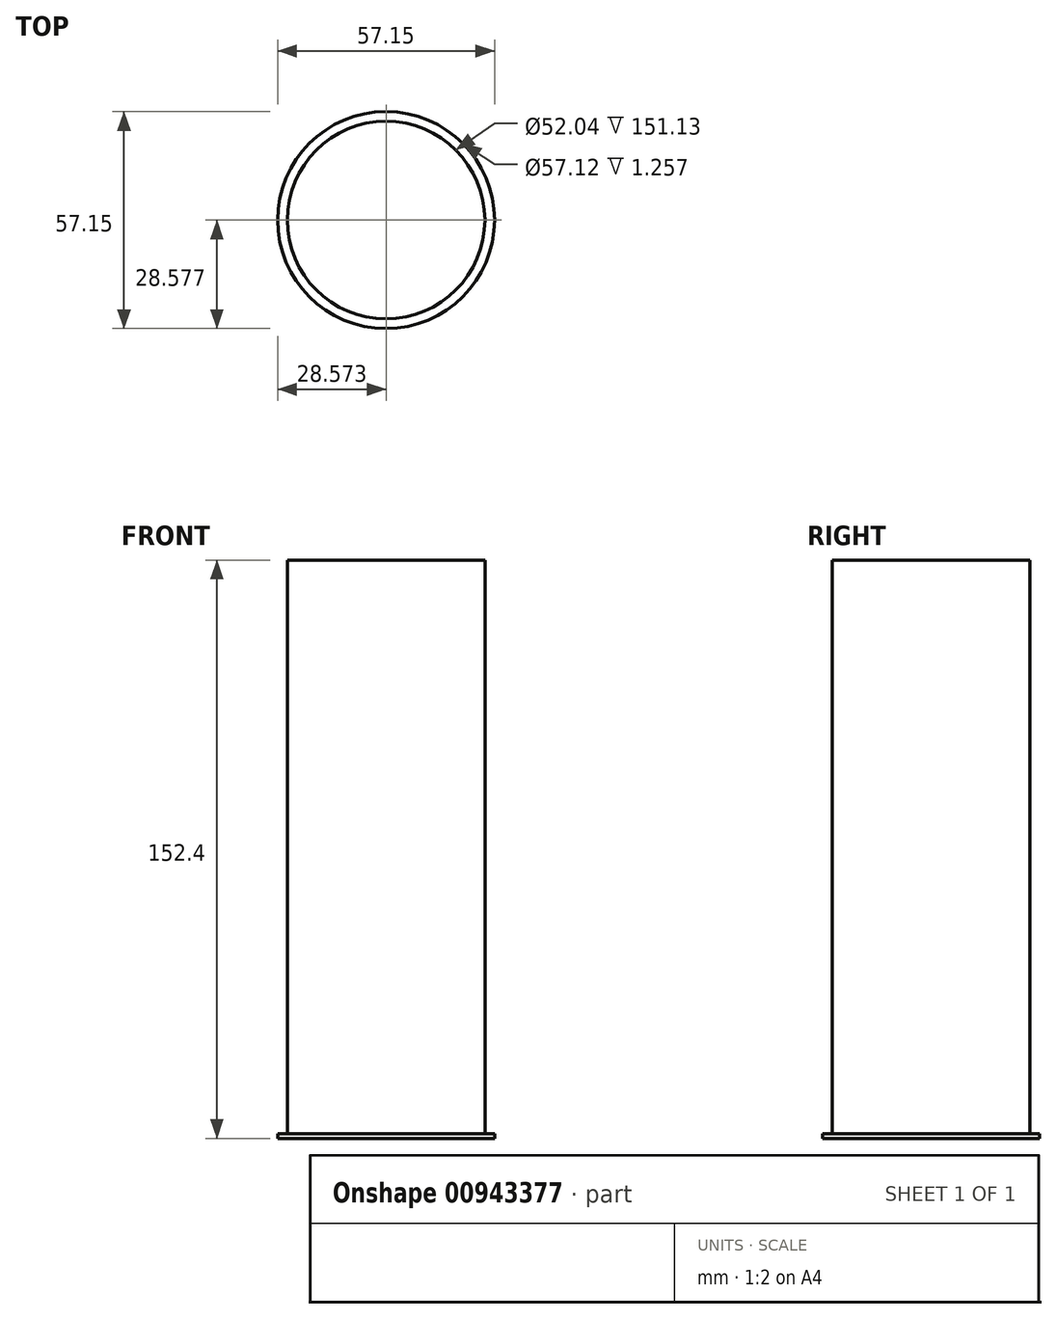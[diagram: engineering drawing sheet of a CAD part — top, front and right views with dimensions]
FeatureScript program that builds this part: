
annotation { "Feature Type Name" : "Feature", "Feature Type Description" : "" }
export const myFeature = defineFeature(function(context is Context, id is Id, definition is map)
    precondition{}
    {
        {
            var Q0;
            Q0=qCreatedBy(makeId("Top.planeOp"),FACE);
            var sketch = newSketch(context, id + "F0", { "sketchPlane" : qUnion([Q0])});
            skCircle(sketch, "E0", {"center": v(-105.37, 105.8) * mm, "radius": 26.04 * mm});
            skCircle(sketch, "E1", {"center": v(-105.37, 105.8) * mm, "radius": 28.58 * mm});
            skSolve(sketch);
        }
        {
            var Q0;
            Q0=makeQuery(id+"F0.imprint","IMPRINT",FACE,{"disambiguationData":[TD([[makeQuery(id+"F0.imprint","IMPRINT",EDGE,{"derivedFrom":sQuery(id+"F0.wireOp",EDGE,"E0")}),1.0]])]});
            extrude(context, id + "F1", {"entities" : qUnion([Q0]), "depth" : 152.4 * mm, "offsetDistance" : 25.4 * mm});
        }
        {
            var Q0;
            Q0 = qSketchRegion(id + "F0", true);
            extrude(context, id + "F2", {"entities" : qUnion([Q0]), "operationType" : NewBodyOperationType.ADD, "depth" : 1.27 * mm, "offsetDistance" : 25.4 * mm});
        }
        {
            var Q0;
            {var subQ0=sQuery(id+"F0.wireOp",EDGE,"E0");Q0=makeQuery(id+"F2.boolean.opBoolean","MERGE",FACE,{"derivedFrom":[makeQuery(id+"F1.opExtrude","CAP_FACE",FACE,{"disambiguationData":[OSD([subQ0])],"isStart":true}),makeQuery(id+"F2.opExtrude","CAP_FACE",FACE,{"disambiguationData":[OSD([subQ0,sQuery(id+"F0.wireOp",EDGE,"E1")])],"isStart":true})]});}
            shell(context, id + "F3", {"entities" : qUnion([Q0]), "thickness" : 0.01 * mm});
        }
    });
